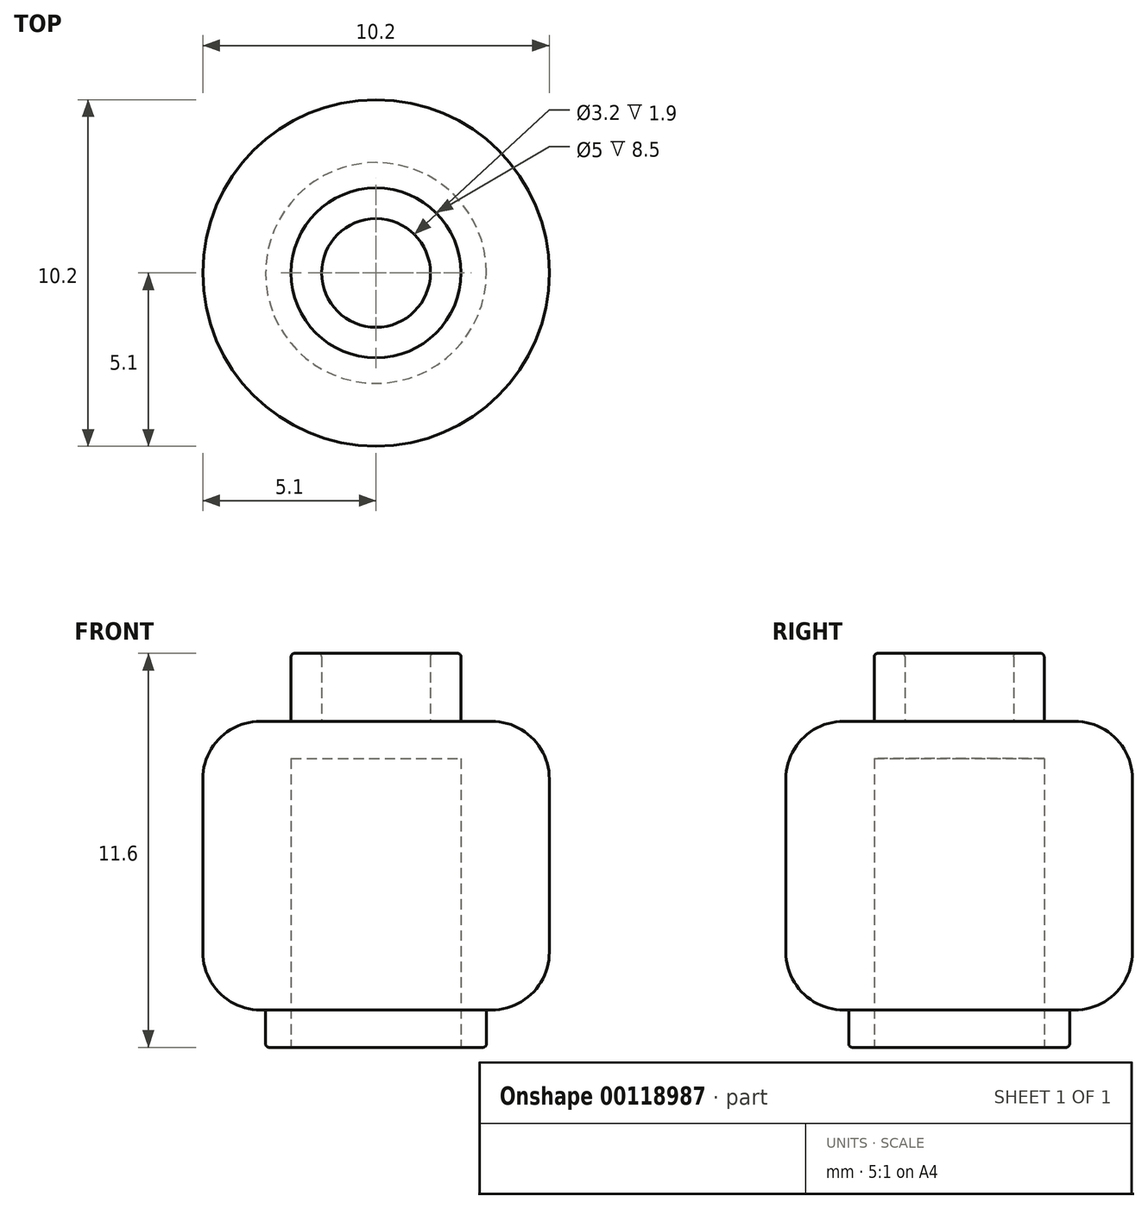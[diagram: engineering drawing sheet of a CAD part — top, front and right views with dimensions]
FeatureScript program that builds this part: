
annotation { "Feature Type Name" : "Feature", "Feature Type Description" : "" }
export const myFeature = defineFeature(function(context is Context, id is Id, definition is map)
    precondition{}
    {
        {
            var Q0;
            Q0=qCreatedBy(makeId("Top.planeOp"),FACE);
            var sketch = newSketch(context, id + "F0", { "sketchPlane" : qUnion([Q0])});
            skCircle(sketch, "E0", {"center": v(0, 0) * mm, "radius": 3.25 * mm});
            skSolve(sketch);
        }
        {
            var Q0;
            Q0=makeQuery(id+"F0.imprint","IMPRINT",FACE,{"disambiguationData":[TD([[makeQuery(id+"F0.imprint","IMPRINT",EDGE,{"derivedFrom":sQuery(id+"F0.wireOp",EDGE,"E0")}),1.0]])]});
            extrude(context, id + "F1", {"entities" : qUnion([Q0]), "depth" : 1.1 * mm});
        }
        {
            var Q0;
            Q0=makeQuery(id+"F1.opExtrude","CAP_FACE",FACE,{"disambiguationData":[OSD([sQuery(id+"F0.wireOp",EDGE,"E0")])],"isStart":false});
            var sketch = newSketch(context, id + "F2", { "sketchPlane" : qUnion([Q0])});
            skCircle(sketch, "E1", {"center": v(0, 0) * mm, "radius": 5.1 * mm});
            skSolve(sketch);
        }
        {
            var Q0;
            Q0 = qSketchRegion(id + "F2", true);
            extrude(context, id + "F3", {"entities" : qUnion([Q0]), "operationType" : NewBodyOperationType.ADD, "depth" : 8.5 * mm});
        }
        {
            var Q0;
            Q0=makeQuery(id+"F3.opExtrude","CAP_FACE",FACE,{"disambiguationData":[OSD([sQuery(id+"F2.wireOp",EDGE,"E1")])],"isStart":false});
            var sketch = newSketch(context, id + "F4", { "sketchPlane" : qUnion([Q0])});
            skCircle(sketch, "E2", {"center": v(0, 0) * mm, "radius": 2.5 * mm});
            skCircle(sketch, "E3", {"center": v(0, 0) * mm, "radius": 1.6 * mm});
            skSolve(sketch);
        }
        {
            var Q0;
            Q0 = qSketchRegion(id + "F4", true);
            extrude(context, id + "F5", {"entities" : qUnion([Q0]), "operationType" : NewBodyOperationType.ADD, "depth" : 2 * mm});
        }
        {
            var Q0;
            Q0=makeQuery(id+"F1.opExtrude","CAP_FACE",FACE,{"disambiguationData":[OSD([sQuery(id+"F0.wireOp",EDGE,"E0")])],"isStart":true});
            var sketch = newSketch(context, id + "F6", { "sketchPlane" : qUnion([Q0])});
            skCircle(sketch, "E4", {"center": v(0, 0) * mm, "radius": 2.5 * mm});
            skSolve(sketch);
        }
        {
            var Q0;
            Q0 = qSketchRegion(id + "F6", true);
            var Q1;
            Q1=makeQuery(id+"F6.imprint","IMPRINT",FACE,{"disambiguationData":[TD([[makeQuery(id+"F6.imprint","IMPRINT",EDGE,{"derivedFrom":sQuery(id+"F6.wireOp",EDGE,"E4")}),1.0]])]});
            extrude(context, id + "F7", {"entities" : qUnion([Q0, Q1]), "operationType" : NewBodyOperationType.REMOVE, "oppositeDirection" : true, "depth" : 8.5 * mm});
        }
        {
            var Q0;
            Q0=makeQuery(id+"F1.opExtrude","CAP_EDGE",EDGE,{"disambiguationData":[OSD([sQuery(id+"F0.wireOp",EDGE,"E0")])],"isStart":true});
            var Q1;
            Q1=makeQuery(id+"F5.opExtrude","CAP_EDGE",EDGE,{"disambiguationData":[OSD([sQuery(id+"F4.wireOp",EDGE,"E2")])],"isStart":false});
            var Q2;
            Q2=makeQuery(id+"F5.opExtrude","CAP_EDGE",EDGE,{"disambiguationData":[OSD([sQuery(id+"F4.wireOp",EDGE,"E3")])],"isStart":false});
            fillet(context, id + "F8", {"entities" : qUnion([Q0, Q1, Q2]), "radius" : 0.1 * mm, "tangentPropagation" : true, "allowEdgeOverflow" : false});
        }
        {
            var Q0;
            Q0=makeQuery(id+"F3.opExtrude","CAP_EDGE",EDGE,{"disambiguationData":[OSD([sQuery(id+"F2.wireOp",EDGE,"E1")])],"isStart":false});
            var Q1;
            Q1=makeQuery(id+"F3.opExtrude","CAP_EDGE",EDGE,{"disambiguationData":[OSD([sQuery(id+"F2.wireOp",EDGE,"E1")])],"isStart":true});
            fillet(context, id + "F9", {"entities" : qUnion([Q0, Q1]), "radius" : 1.7 * mm, "tangentPropagation" : true, "allowEdgeOverflow" : false});
        }
    });
